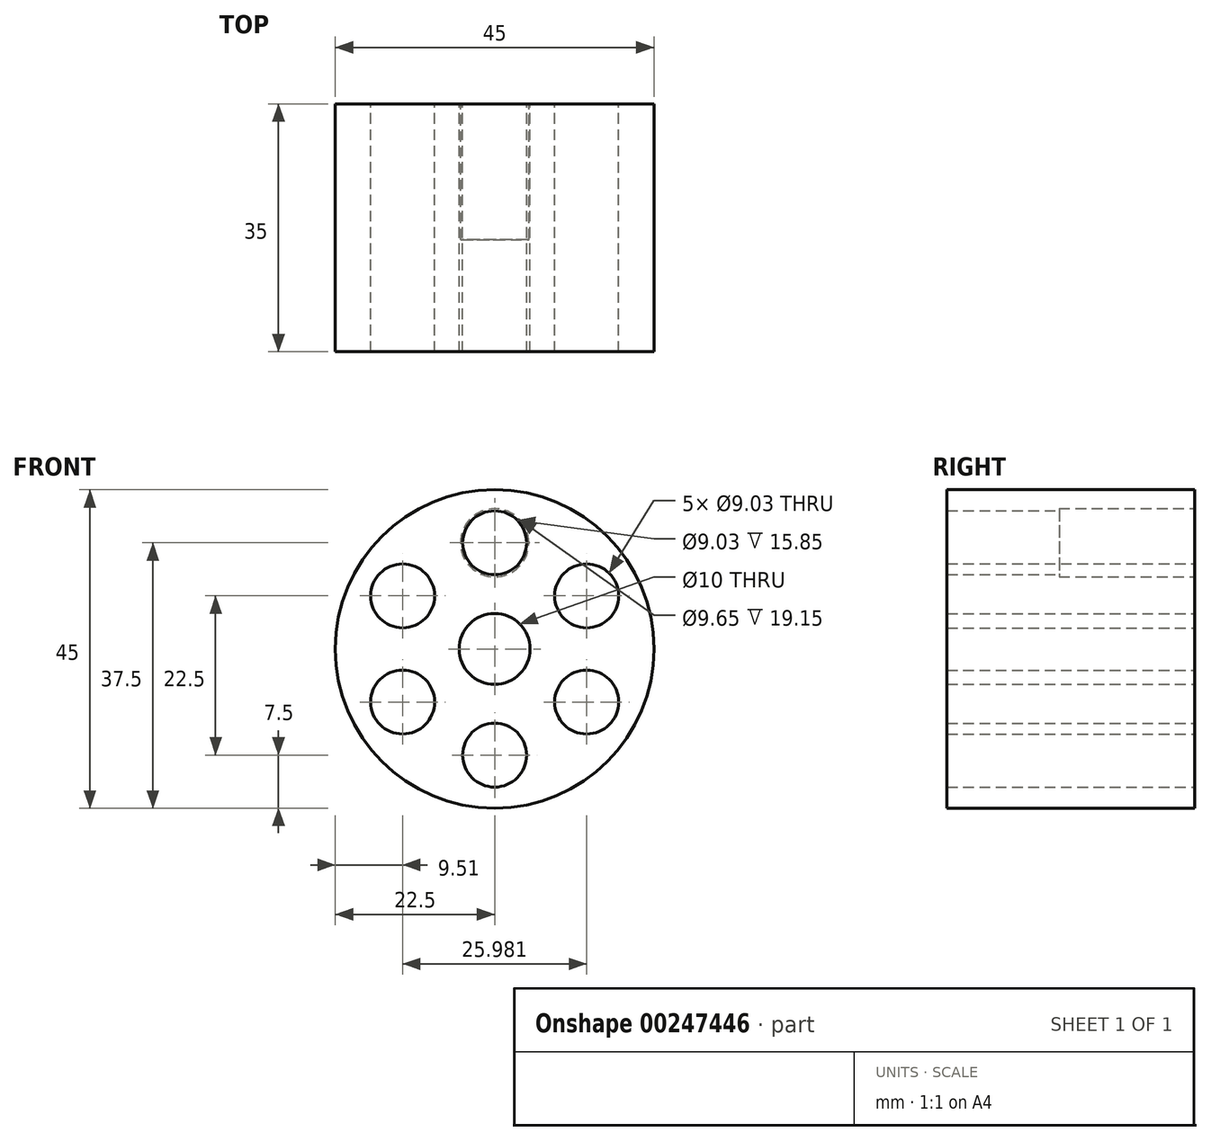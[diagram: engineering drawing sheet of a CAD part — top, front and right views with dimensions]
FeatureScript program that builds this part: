
annotation { "Feature Type Name" : "Feature", "Feature Type Description" : "" }
export const myFeature = defineFeature(function(context is Context, id is Id, definition is map)
    precondition{}
    {
        {
            var Q0;
            Q0=qCreatedBy(makeId("Front.planeOp"),FACE);
            var sketch = newSketch(context, id + "F0", { "sketchPlane" : qUnion([Q0])});
            skCircle(sketch, "E0", {"center": v(0, 0) * mm, "radius": 22.5 * mm});
            skCircle(sketch, "E1", {"center": v(0, 15) * mm, "radius": 4.51 * mm});
            skCircle(sketch, "E2", {"center": v(0, 0) * mm, "radius": 5 * mm});
            skCircle(sketch, "E3.1.0", {"center": v(-13, 7.5) * mm, "radius": 4.51 * mm});
            skCircle(sketch, "E3.2.0", {"center": v(-13, -7.5) * mm, "radius": 4.51 * mm});
            skCircle(sketch, "E3.3.0", {"center": v(0, -15) * mm, "radius": 4.51 * mm});
            skCircle(sketch, "E3.4.0", {"center": v(13, -7.5) * mm, "radius": 4.51 * mm});
            skCircle(sketch, "E3.5.0", {"center": v(13, 7.5) * mm, "radius": 4.51 * mm});
            skSolve(sketch);
        }
        {
            var Q0;
            Q0=makeQuery(id+"F0.imprint","IMPRINT",FACE,{"disambiguationData":[TD([[makeQuery(id+"F0.imprint","IMPRINT",EDGE,{"derivedFrom":sQuery(id+"F0.wireOp",EDGE,"E0")}),1.0]])]});
            extrude(context, id + "F1", {"entities" : qUnion([Q0]), "endBound" : BoundingType.SYMMETRIC, "depth" : 35 * mm});
        }
        {
            var Q0;
            Q0=makeQuery(id+"F1.opExtrude","CAP_FACE",FACE,{"disambiguationData":[OSD([sQuery(id+"F0.wireOp",EDGE,"E0"),sQuery(id+"F0.wireOp",EDGE,"E1"),sQuery(id+"F0.wireOp",EDGE,"E2"),sQuery(id+"F0.wireOp",EDGE,"E3.1.0"),sQuery(id+"F0.wireOp",EDGE,"E3.2.0"),sQuery(id+"F0.wireOp",EDGE,"E3.3.0"),sQuery(id+"F0.wireOp",EDGE,"E3.4.0"),sQuery(id+"F0.wireOp",EDGE,"E3.5.0")])],"isStart":true});
            var sketch = newSketch(context, id + "F2", { "sketchPlane" : qUnion([Q0])});
            skCircle(sketch, "E4", {"center": v(0, 15) * mm, "radius": 4.83 * mm});
            skSolve(sketch);
        }
        {
            var Q0;
            Q0 = qSketchRegion(id + "F2", true);
            extrude(context, id + "F3", {"entities" : qUnion([Q0]), "operationType" : NewBodyOperationType.REMOVE, "oppositeDirection" : true, "depth" : 19.15 * mm});
        }
    });
